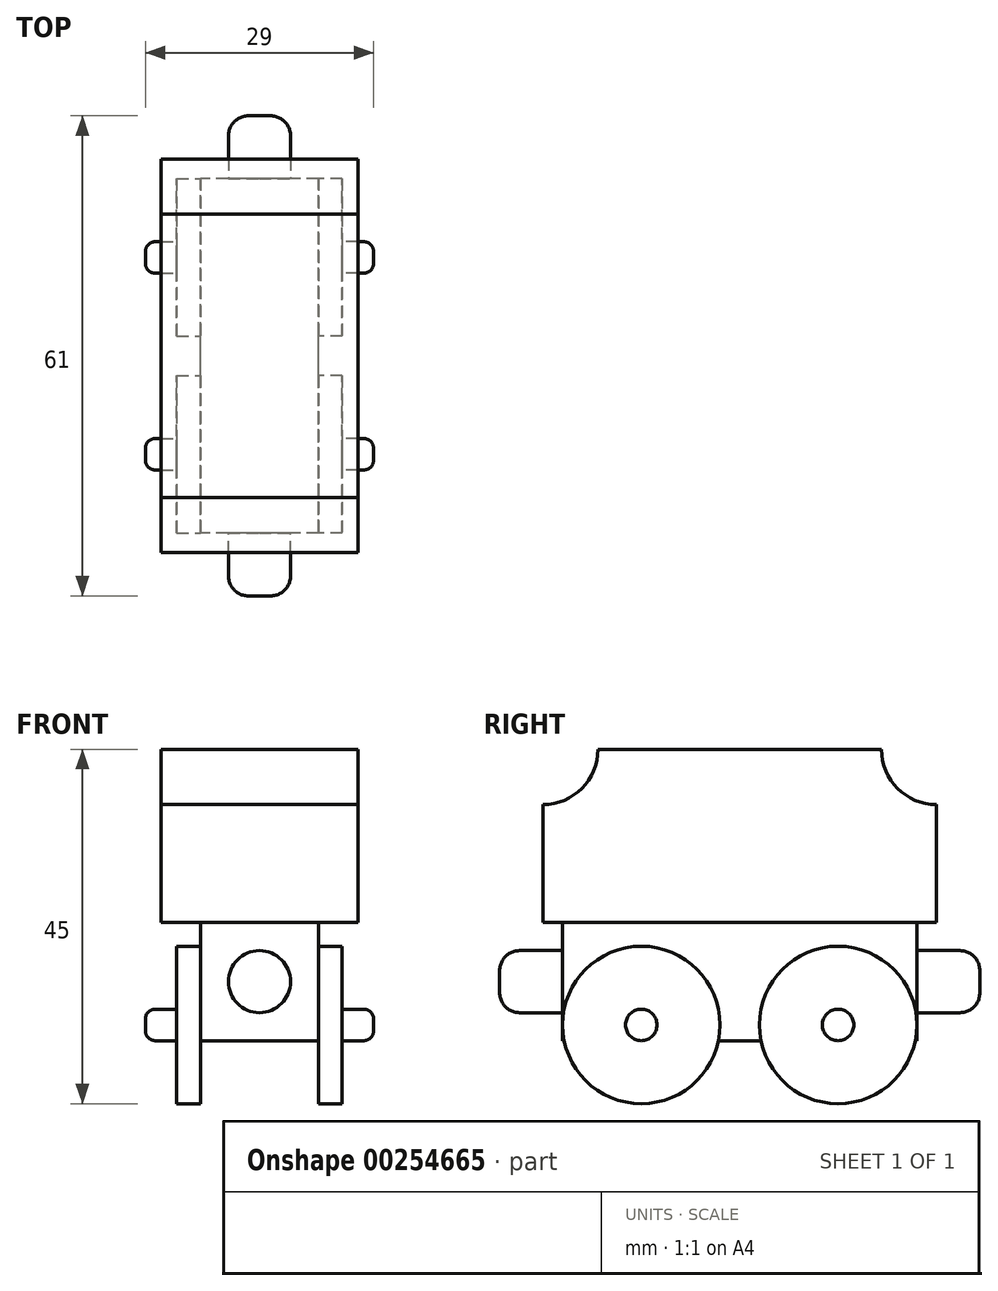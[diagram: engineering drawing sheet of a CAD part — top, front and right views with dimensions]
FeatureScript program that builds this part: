
annotation { "Feature Type Name" : "Feature", "Feature Type Description" : "" }
export const myFeature = defineFeature(function(context is Context, id is Id, definition is map)
    precondition{}
    {
        {
            var Q0;
            Q0=qCreatedBy(makeId("Front.planeOp"),FACE);
            var sketch = newSketch(context, id + "F0", { "sketchPlane" : qUnion([Q0])});
            skLineSegment(sketch, "E0.bottom", {"start": v(7.5, 7.5) * mm, "end": v(-7.5, 7.5) * mm});
            skLineSegment(sketch, "E0.top", {"start": v(7.5, -7.5) * mm, "end": v(-7.5, -7.5) * mm});
            skLineSegment(sketch, "E0.left", {"start": v(7.5, 7.5) * mm, "end": v(7.5, -7.5) * mm});
            skLineSegment(sketch, "E0.right", {"start": v(-7.5, 7.5) * mm, "end": v(-7.5, -7.5) * mm});
            skPoint(sketch, "E0.middle", {"position": v(0, 0) * mm});
            skSolve(sketch);
        }
        {
            var Q0;
            Q0 = qSketchRegion(id + "F0", true);
            extrude(context, id + "F1", {"entities" : qUnion([Q0]), "endBound" : BoundingType.SYMMETRIC, "depth" : 45 * mm});
        }
        {
            var Q0;
            Q0=qCreatedBy(makeId("Right.planeOp"),FACE);
            var sketch = newSketch(context, id + "F2", { "sketchPlane" : qUnion([Q0])});
            skLineSegment(sketch, "E1.bottom", {"start": v(-25, 7.5) * mm, "end": v(25, 7.5) * mm});
            skLineSegment(sketch, "E1.top", {"start": v(-25, 29.5) * mm, "end": v(25, 29.5) * mm});
            skLineSegment(sketch, "E1.left", {"start": v(-25, 7.5) * mm, "end": v(-25, 29.5) * mm});
            skLineSegment(sketch, "E1.right", {"start": v(25, 7.5) * mm, "end": v(25, 29.5) * mm});
            skPoint(sketch, "E1.middle", {"position": v(0, 18.5) * mm});
            skSolve(sketch);
        }
        {
            var Q0;
            Q0 = qSketchRegion(id + "F2", true);
            extrude(context, id + "F3", {"entities" : qUnion([Q0]), "operationType" : NewBodyOperationType.ADD, "endBound" : BoundingType.SYMMETRIC, "depth" : 25 * mm});
        }
        {
            var Q0;
            Q0=qCreatedBy(makeId("Right.planeOp"),FACE);
            var sketch = newSketch(context, id + "F4", { "sketchPlane" : qUnion([Q0])});
            skArc(sketch, "E2", {"start": v(-25, 22.5) * mm, "mid": v(-20.05, 24.55) * mm, "end": v(-18, 29.5) * mm});
            skArc(sketch, "E3.MirrorCS", {"start": v(25, 22.5) * mm, "mid": v(20.05, 24.55) * mm, "end": v(18, 29.5) * mm});
            skLineSegment(sketch, "E4", {"start": v(-25, 22.5) * mm, "end": v(-25, 29.5) * mm});
            skLineSegment(sketch, "E5", {"start": v(-25, 29.5) * mm, "end": v(-18, 29.5) * mm});
            skLineSegment(sketch, "E6", {"start": v(18, 29.5) * mm, "end": v(25, 29.5) * mm});
            skLineSegment(sketch, "E7", {"start": v(25, 22.5) * mm, "end": v(25, 29.5) * mm});
            skSolve(sketch);
        }
        {
            var Q0;
            Q0 = qSketchRegion(id + "F4", true);
            extrude(context, id + "F5", {"entities" : qUnion([Q0]), "operationType" : NewBodyOperationType.REMOVE, "endBound" : BoundingType.SYMMETRIC, "oppositeDirection" : true, "depth" : 25.4 * mm});
        }
        {
            var Q0;
            Q0=makeQuery(id+"F1.opExtrude","SWEPT_FACE",FACE,{"disambiguationData":[OSD([sQuery(id+"F0.wireOp",EDGE,"E0.left")])]});
            var sketch = newSketch(context, id + "F6", { "sketchPlane" : qUnion([Q0])});
            skCircle(sketch, "E8", {"center": v(12.5, -5.5) * mm, "radius": 10 * mm});
            skCircle(sketch, "E9", {"center": v(-12.5, -5.5) * mm, "radius": 10 * mm});
            skSolve(sketch);
        }
        {
            var Q0;
            Q0 = qSketchRegion(id + "F6", true);
            extrude(context, id + "F7", {"entities" : qUnion([Q0]), "operationType" : NewBodyOperationType.ADD, "depth" : 3 * mm});
        }
        {
            var Q0;
            Q0=makeQuery(id+"F7.opExtrude","CAP_FACE",FACE,{"disambiguationData":[OSD([sQuery(id+"F6.wireOp",EDGE,"E8")])],"isStart":false});
            var sketch = newSketch(context, id + "F8", { "sketchPlane" : qUnion([Q0])});
            skCircle(sketch, "E10", {"center": v(12.5, -5.5) * mm, "radius": 2 * mm});
            skSolve(sketch);
        }
        {
            var Q0;
            Q0 = qSketchRegion(id + "F8", true);
            extrude(context, id + "F9", {"entities" : qUnion([Q0]), "operationType" : NewBodyOperationType.ADD, "depth" : 4 * mm});
        }
        {
            var Q0;
            Q0=makeQuery(id+"F9.opExtrude","CAP_EDGE",EDGE,{"disambiguationData":[OSD([sQuery(id+"F8.wireOp",EDGE,"E10")])],"isStart":false});
            fillet(context, id + "F10", {"entities" : qUnion([Q0]), "radius" : 1.27 * mm, "tangentPropagation" : true, "allowEdgeOverflow" : false});
        }
        {
            var Q0;
            Q0=makeQuery(id+"F1.opExtrude","CAP_FACE",FACE,{"disambiguationData":[OSD([sQuery(id+"F0.wireOp",EDGE,"E0.bottom"),sQuery(id+"F0.wireOp",EDGE,"E0.top"),sQuery(id+"F0.wireOp",EDGE,"E0.left"),sQuery(id+"F0.wireOp",EDGE,"E0.right")])],"isStart":true});
            var sketch = newSketch(context, id + "F11", { "sketchPlane" : qUnion([Q0])});
            skCircle(sketch, "E11", {"center": v(0, 0) * mm, "radius": 3.94 * mm});
            skSolve(sketch);
        }
        {
            var Q0;
            Q0 = qSketchRegion(id + "F11", true);
            extrude(context, id + "F12", {"entities" : qUnion([Q0]), "operationType" : NewBodyOperationType.ADD, "depth" : 8 * mm});
        }
        {
            var Q0;
            Q0=makeQuery(id+"F12.opExtrude","CAP_EDGE",EDGE,{"disambiguationData":[OSD([sQuery(id+"F11.wireOp",EDGE,"E11")])],"isStart":false});
            fillet(context, id + "F13", {"entities" : qUnion([Q0]), "radius" : 2.54 * mm, "tangentPropagation" : true, "allowEdgeOverflow" : false});
        }
        {
            var Q0;
            Q0=makeQuery(id+"F1.opExtrude","SWEPT_BODY",BODY,{"disambiguationData":[OSD([sQuery(id+"F0.wireOp",EDGE,"E0.bottom"),sQuery(id+"F0.wireOp",EDGE,"E0.top"),sQuery(id+"F0.wireOp",EDGE,"E0.left"),sQuery(id+"F0.wireOp",EDGE,"E0.right")])]});
            var Q1;
            Q1=qCreatedBy(makeId("Right.planeOp"),FACE);
            mirror(context, id + "F14", {"operationType" : NewBodyOperationType.ADD, "entities" : qUnion([Q0]), "mirrorPlane" : qUnion([Q1])});
        }
        {
            var Q0;
            Q0=makeQuery(id+"F1.opExtrude","SWEPT_BODY",BODY,{"disambiguationData":[OSD([sQuery(id+"F0.wireOp",EDGE,"E0.bottom"),sQuery(id+"F0.wireOp",EDGE,"E0.top"),sQuery(id+"F0.wireOp",EDGE,"E0.left"),sQuery(id+"F0.wireOp",EDGE,"E0.right")])]});
            var Q1;
            Q1=qCreatedBy(makeId("Front.planeOp"),FACE);
            mirror(context, id + "F15", {"operationType" : NewBodyOperationType.ADD, "entities" : qUnion([Q0]), "mirrorPlane" : qUnion([Q1])});
        }
    });
